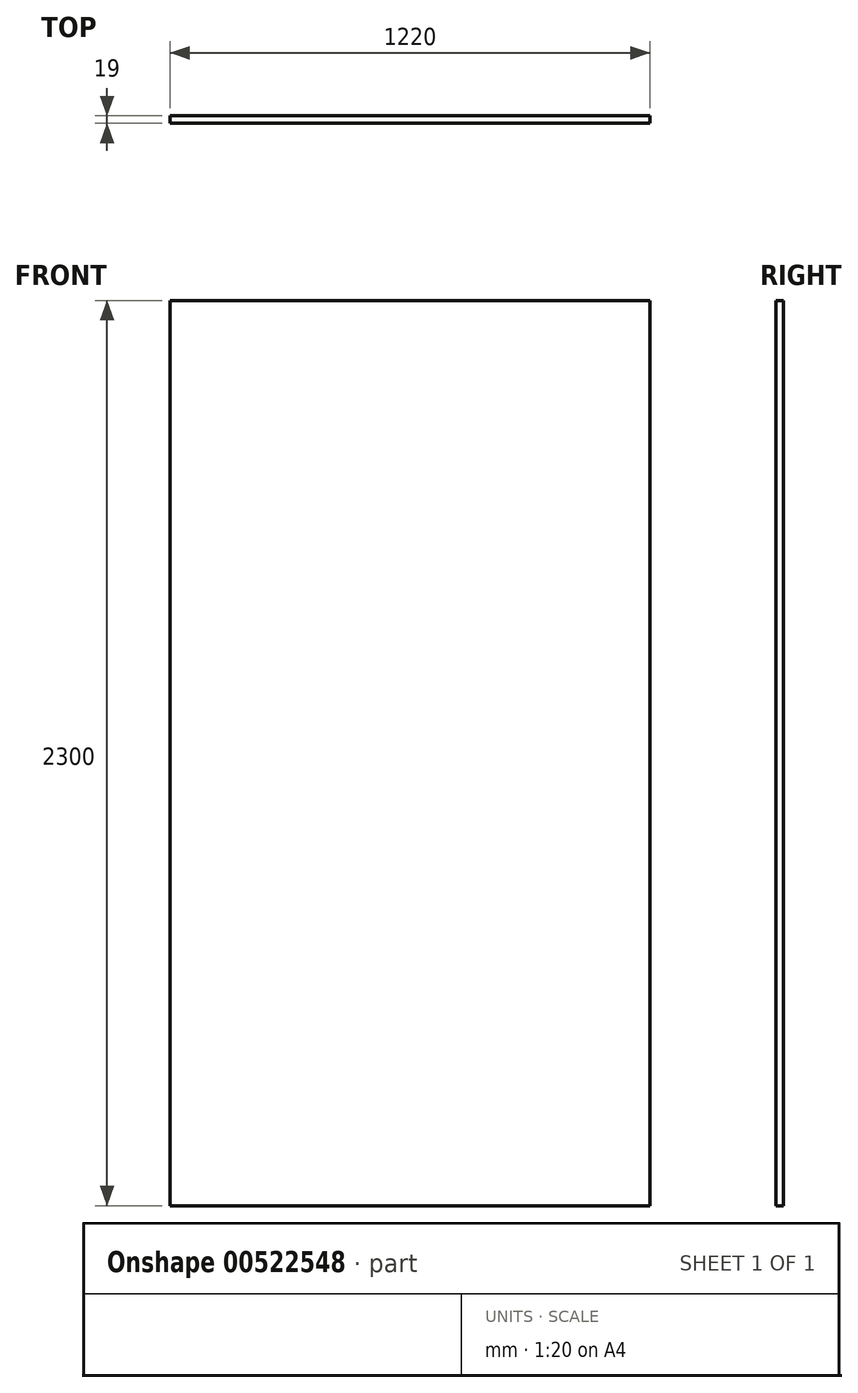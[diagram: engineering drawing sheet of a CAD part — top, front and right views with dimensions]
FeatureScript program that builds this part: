
annotation { "Feature Type Name" : "Feature", "Feature Type Description" : "" }
export const myFeature = defineFeature(function(context is Context, id is Id, definition is map)
    precondition{}
    {
        {
            var Q0;
            Q0=qCreatedBy(makeId("Front.planeOp"),FACE);
            var sketch = newSketch(context, id + "F0", { "sketchPlane" : qUnion([Q0])});
            skLineSegment(sketch, "E0.bottom", {"start": v(-1172.73, 2282.75) * mm, "end": v(47.27, 2282.75) * mm});
            skLineSegment(sketch, "E0.top", {"start": v(-1172.73, -17.25) * mm, "end": v(47.27, -17.25) * mm});
            skLineSegment(sketch, "E0.left", {"start": v(-1172.73, 2282.75) * mm, "end": v(-1172.73, -17.25) * mm});
            skLineSegment(sketch, "E0.right", {"start": v(47.27, 2282.75) * mm, "end": v(47.27, -17.25) * mm});
            skSolve(sketch);
        }
        {
            var Q0;
            Q0 = qSketchRegion(id + "F0", true);
            extrude(context, id + "F1", {"entities" : qUnion([Q0]), "depth" : 19 * mm, "offsetDistance" : 25 * mm});
        }
    });
